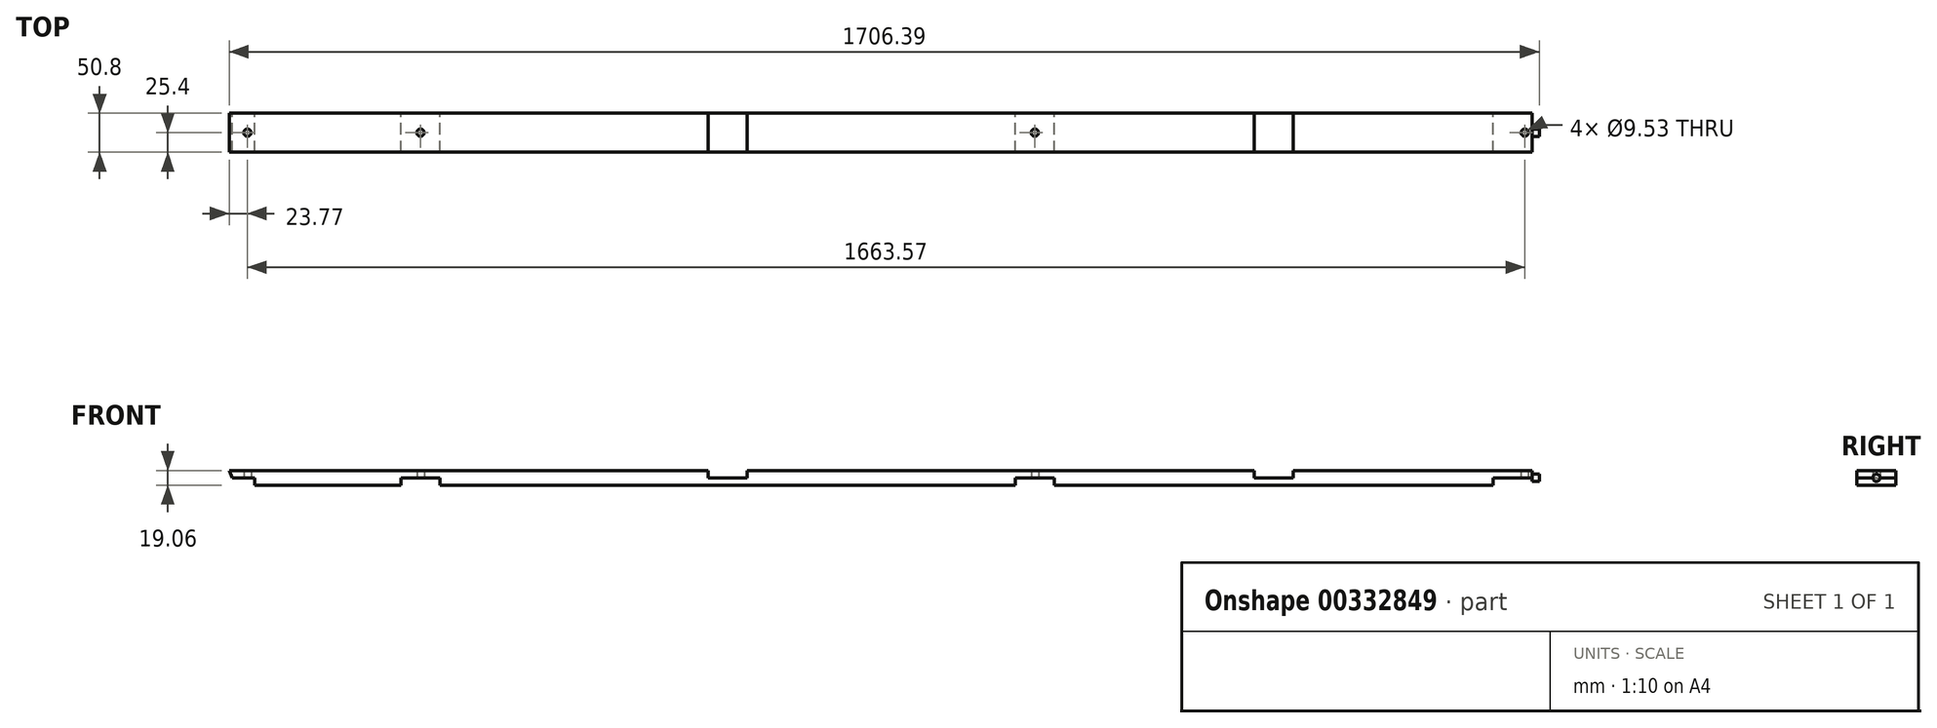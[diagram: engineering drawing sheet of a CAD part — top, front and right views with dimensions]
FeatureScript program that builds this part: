
annotation { "Feature Type Name" : "Feature", "Feature Type Description" : "" }
export const myFeature = defineFeature(function(context is Context, id is Id, definition is map)
    precondition{}
    {
        {
            var Q0;
            Q0=qCreatedBy(makeId("Front.planeOp"),FACE);
            var sketch = newSketch(context, id + "F0", { "sketchPlane" : qUnion([Q0])});
            skLineSegment(sketch, "E0.bottom", {"start": v(29.35, -9.53) * mm, "end": v(219.85, -9.53) * mm});
            skLineSegment(sketch, "E0.right", {"start": v(1693.05, 0) * mm, "end": v(1693.05, 9.52) * mm});
            skLineSegment(sketch, "E1", {"start": v(1693.05, 9.52) * mm, "end": v(-3.95, 9.52) * mm});
            skLineSegment(sketch, "E2.top", {"start": v(0, 0) * mm, "end": v(29.35, 0) * mm});
            skLineSegment(sketch, "E2.right", {"start": v(29.35, -9.53) * mm, "end": v(29.35, 0) * mm});
            skLineSegment(sketch, "E3.top", {"start": v(219.85, 0) * mm, "end": v(270.65, 0) * mm});
            skLineSegment(sketch, "E3.left", {"start": v(219.85, -9.53) * mm, "end": v(219.85, 0) * mm});
            skLineSegment(sketch, "E3.right", {"start": v(270.65, -9.53) * mm, "end": v(270.65, 0) * mm});
            skLineSegment(sketch, "E4.trimOffspring", {"start": v(270.65, -9.53) * mm, "end": v(1019.95, -9.53) * mm});
            skLineSegment(sketch, "E5.top", {"start": v(1019.95, 0) * mm, "end": v(1070.75, 0) * mm});
            skLineSegment(sketch, "E5.left", {"start": v(1019.95, -9.53) * mm, "end": v(1019.95, 0) * mm});
            skLineSegment(sketch, "E5.right", {"start": v(1070.75, -9.53) * mm, "end": v(1070.75, 0) * mm});
            skLineSegment(sketch, "E6.trimOffspring", {"start": v(1070.75, -9.53) * mm, "end": v(1642.25, -9.53) * mm});
            skLineSegment(sketch, "E7.top", {"start": v(1642.25, 0) * mm, "end": v(1693.05, 0) * mm});
            skLineSegment(sketch, "E7.left", {"start": v(1642.25, -9.53) * mm, "end": v(1642.25, 0) * mm});
            skPoint(sketch, "E8.orphan", {"position": v(1693.05, -9.53) * mm});
            skLineSegment(sketch, "E9", {"start": v(645.3, -9.53) * mm, "end": v(645.3, 9.52) * mm, "construction": true});
            skLineSegment(sketch, "E10", {"start": v(-3.95, 9.52) * mm, "end": v(0, 0) * mm});
            skSolve(sketch);
        }
        {
            var Q0;
            Q0=makeQuery(id+"F0.imprint","IMPRINT",FACE,{"disambiguationData":[TD([[makeQuery(id+"F0.imprint","IMPRINT",EDGE,{"derivedFrom":sQuery(id+"F0.wireOp",EDGE,"E0.bottom")}),1.0]])]});
            extrude(context, id + "F1", {"entities" : qUnion([Q0]), "endBound" : BoundingType.SYMMETRIC, "depth" : 50.8 * mm});
        }
        {
            var Q0;
            Q0=qCreatedBy(makeId("Right.planeOp"),FACE);
            cPlane(context, id + "F2", {"entities" : qUnion([Q0]), "cplaneType" : CPlaneType.OFFSET, "offset" : 1692.9 * mm, "width" : 152.4 * mm, "height" : 152.4 * mm});
        }
        {
            var Q0;
            Q0=qCreatedBy(id+"F2.planeOp",FACE);
            var sketch = newSketch(context, id + "F3", { "sketchPlane" : qUnion([Q0])});
            skCircle(sketch, "E11", {"center": v(0, 0) * mm, "radius": 4.76 * mm});
            skSolve(sketch);
        }
        {
            var Q0;
            Q0 = qSketchRegion(id + "F3", true);
            extrude(context, id + "F4", {"entities" : qUnion([Q0]), "operationType" : NewBodyOperationType.ADD, "depth" : 9.52 * mm});
        }
        {
            var Q0;
            Q0=qCreatedBy(makeId("Top.planeOp"),FACE);
            var sketch = newSketch(context, id + "F5", { "sketchPlane" : qUnion([Q0])});
            skCircle(sketch, "E12", {"center": v(245.25, 0) * mm, "radius": 4.76 * mm});
            skCircle(sketch, "E13", {"center": v(1045.35, 0) * mm, "radius": 4.76 * mm});
            skCircle(sketch, "E14", {"center": v(1683.39, 0) * mm, "radius": 4.76 * mm});
            skCircle(sketch, "E15", {"center": v(19.82, 0) * mm, "radius": 4.76 * mm});
            skSolve(sketch);
        }
        {
            var Q0;
            Q0 = qSketchRegion(id + "F5", true);
            extrude(context, id + "F6", {"entities" : qUnion([Q0]), "operationType" : NewBodyOperationType.REMOVE, "depth" : 25.4 * mm});
        }
        {
            var Q0;
            Q0=qCreatedBy(makeId("Top.planeOp"),FACE);
            var sketch = newSketch(context, id + "F7", { "sketchPlane" : qUnion([Q0])});
            skLineSegment(sketch, "E16", {"start": v(645.3, 267.88) * mm, "end": v(645.3, -144.64) * mm, "construction": true});
            skLineSegment(sketch, "E17.bottom", {"start": v(670.7, -61.6) * mm, "end": v(619.9, -61.6) * mm});
            skLineSegment(sketch, "E17.top", {"start": v(670.7, 252.6) * mm, "end": v(619.9, 252.6) * mm});
            skLineSegment(sketch, "E17.left", {"start": v(670.7, -61.6) * mm, "end": v(670.7, 252.6) * mm});
            skLineSegment(sketch, "E17.right", {"start": v(619.9, -61.6) * mm, "end": v(619.9, 252.6) * mm});
            skPoint(sketch, "E17.middle", {"position": v(645.3, 95.5) * mm});
            skLineSegment(sketch, "E18", {"start": v(1356.5, 259.16) * mm, "end": v(1356.5, -214.72) * mm, "construction": true});
            skLineSegment(sketch, "E19.bottom", {"start": v(1381.9, 62.34) * mm, "end": v(1331.1, 62.34) * mm});
            skLineSegment(sketch, "E19.top", {"start": v(1381.9, -72.05) * mm, "end": v(1331.1, -72.05) * mm});
            skLineSegment(sketch, "E19.left", {"start": v(1381.9, 62.34) * mm, "end": v(1381.9, -72.05) * mm});
            skLineSegment(sketch, "E19.right", {"start": v(1331.1, 62.34) * mm, "end": v(1331.1, -72.05) * mm});
            skPoint(sketch, "E19.middle", {"position": v(1356.5, -4.85) * mm});
            skSolve(sketch);
        }
        {
            var Q0;
            Q0 = qSketchRegion(id + "F7", true);
            extrude(context, id + "F8", {"entities" : qUnion([Q0]), "operationType" : NewBodyOperationType.REMOVE, "depth" : 25.4 * mm});
        }
    });
